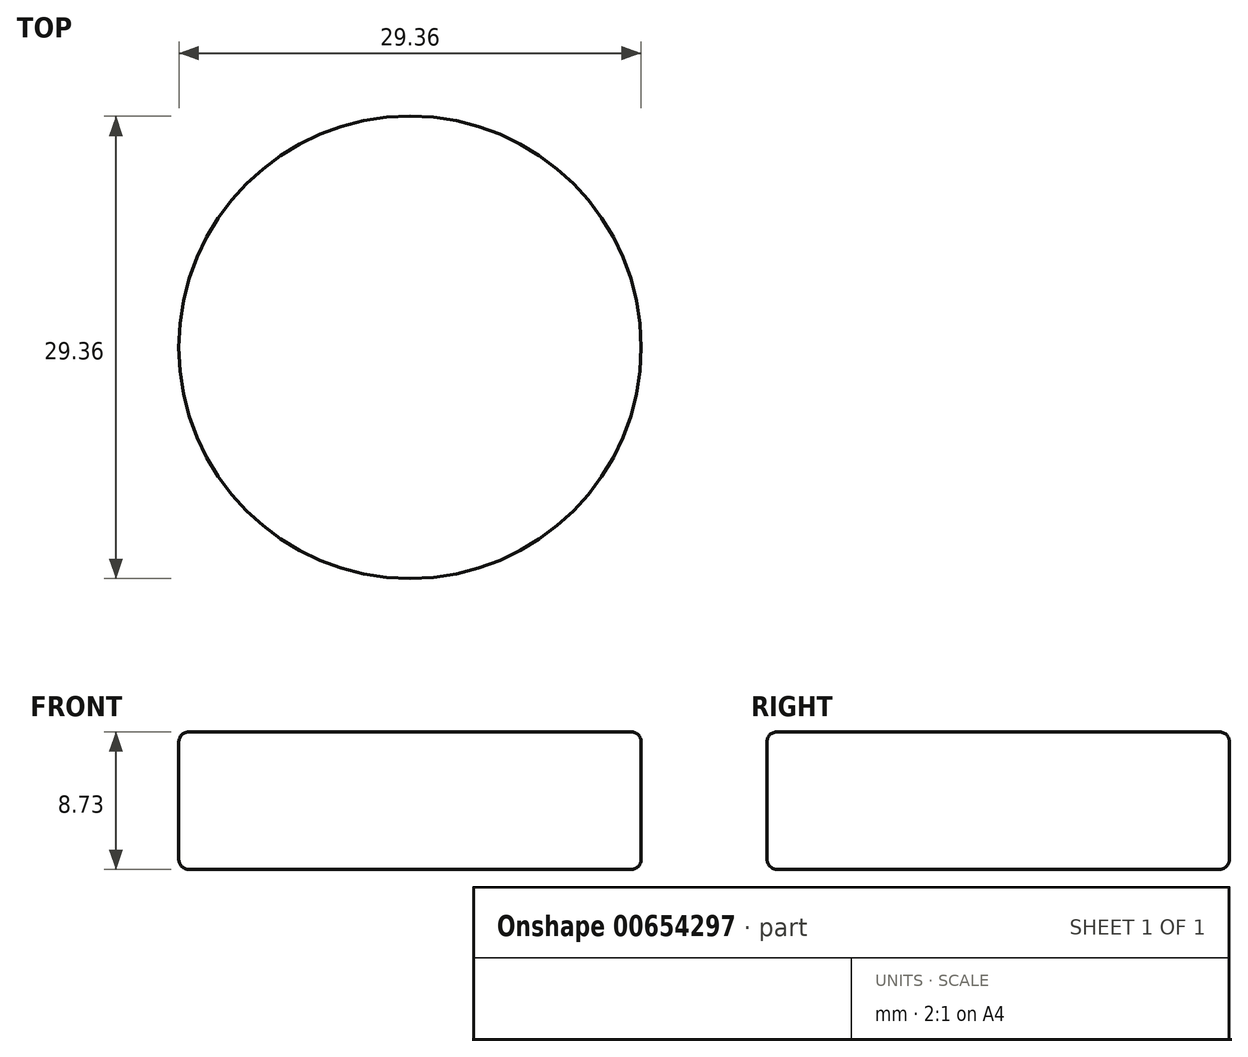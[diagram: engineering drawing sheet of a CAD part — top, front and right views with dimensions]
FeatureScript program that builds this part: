
annotation { "Feature Type Name" : "Feature", "Feature Type Description" : "" }
export const myFeature = defineFeature(function(context is Context, id is Id, definition is map)
    precondition{}
    {
        {
            var Q0;
            Q0=qCreatedBy(makeId("Top.planeOp"),FACE);
            var sketch = newSketch(context, id + "F0", { "sketchPlane" : qUnion([Q0])});
            skCircle(sketch, "E0", {"center": v(0, 0) * mm, "radius": 14.68 * mm});
            skSolve(sketch);
        }
        {
            var Q0;
            Q0=makeQuery(id+"F0.imprint","IMPRINT",FACE,{"disambiguationData":[TD([[makeQuery(id+"F0.imprint","IMPRINT",EDGE,{"derivedFrom":sQuery(id+"F0.wireOp",EDGE,"E0")}),1.0]])]});
            var Q1;
            Q1=sQuery(id+"F0.wireOp",EDGE,"E0");
            extrude(context, id + "F1", {"entities" : qUnion([Q0]), "surfaceEntities" : qUnion([Q1]), "depth" : 8.73 * mm, "offsetDistance" : 25.4 * mm});
        }
        {
            var Q0;
            Q0=makeQuery(id+"F1.opExtrude","CAP_EDGE",EDGE,{"disambiguationData":[OSD([sQuery(id+"F0.wireOp",EDGE,"E0")])],"isStart":false});
            var Q1;
            Q1=makeQuery(id+"F1.opExtrude","CAP_EDGE",EDGE,{"disambiguationData":[OSD([sQuery(id+"F0.wireOp",EDGE,"E0")])],"isStart":true});
            fillet(context, id + "F2", {"entities" : qUnion([Q0, Q1]), "radius" : 0.64 * mm, "tangentPropagation" : true, "allowEdgeOverflow" : false});
        }
    });
